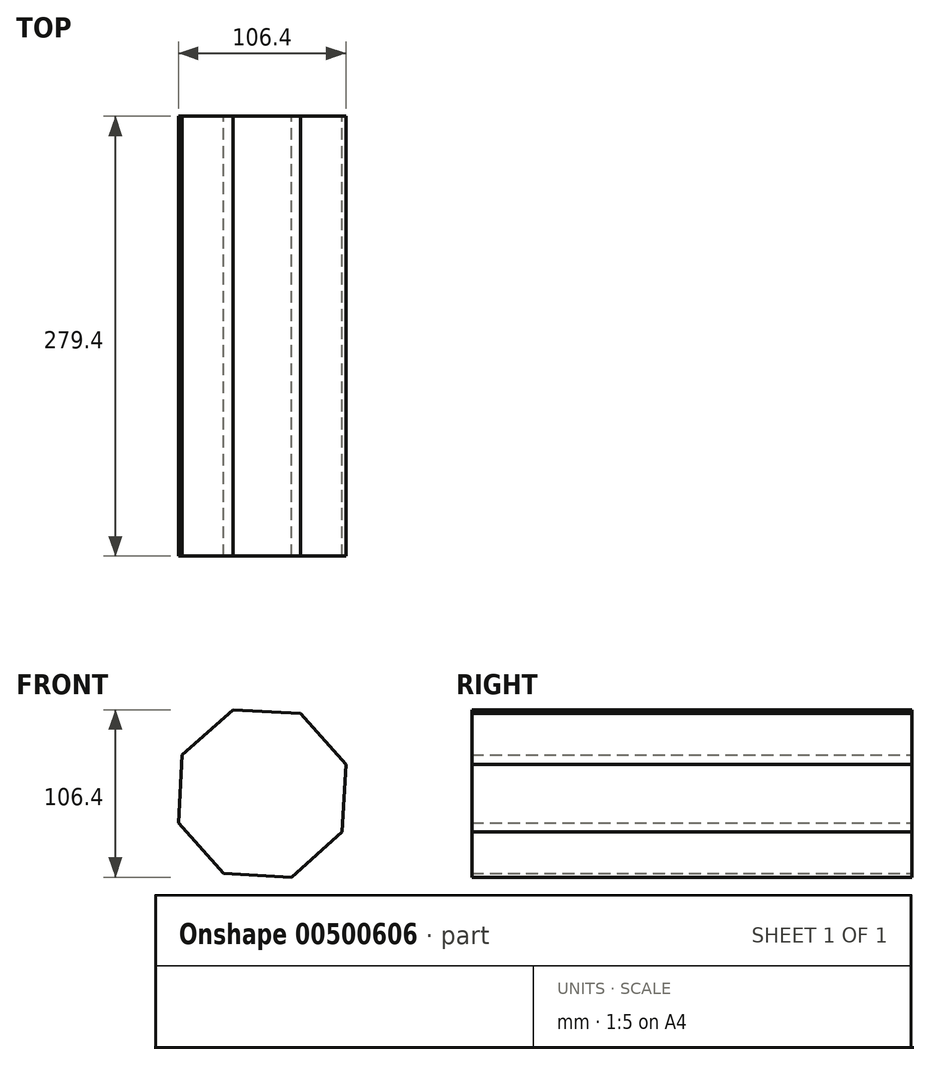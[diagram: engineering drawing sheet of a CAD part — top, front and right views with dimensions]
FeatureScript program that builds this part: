
annotation { "Feature Type Name" : "Feature", "Feature Type Description" : "" }
export const myFeature = defineFeature(function(context is Context, id is Id, definition is map)
    precondition{}
    {
        {
            var Q0;
            Q0=qCreatedBy(makeId("Front.planeOp"),FACE);
            var sketch = newSketch(context, id + "F0", { "sketchPlane" : qUnion([Q0])});
            skCircle(sketch, "E0.cCircle", {"center": v(0, 8.27) * mm, "radius": 56.35 * mm, "construction": true});
            skLineSegment(sketch, "E0.0", {"start": v(-18.58, 61.47) * mm, "end": v(24.48, 59.02) * mm});
            skLineSegment(sketch, "E0.1", {"start": v(24.48, 59.02) * mm, "end": v(53.2, 26.85) * mm});
            skLineSegment(sketch, "E0.2", {"start": v(53.2, 26.85) * mm, "end": v(50.75, -16.21) * mm});
            skLineSegment(sketch, "E0.3", {"start": v(50.75, -16.21) * mm, "end": v(18.58, -44.93) * mm});
            skLineSegment(sketch, "E0.4", {"start": v(18.58, -44.93) * mm, "end": v(-24.48, -42.48) * mm});
            skLineSegment(sketch, "E0.5", {"start": v(-24.48, -42.48) * mm, "end": v(-53.2, -10.3) * mm});
            skLineSegment(sketch, "E0.6", {"start": v(-53.2, -10.3) * mm, "end": v(-50.75, 32.75) * mm});
            skLineSegment(sketch, "E0.7", {"start": v(-50.75, 32.75) * mm, "end": v(-18.58, 61.47) * mm});
            skSolve(sketch);
        }
        {
            var Q0;
            Q0 = qSketchRegion(id + "F0", true);
            extrude(context, id + "F1", {"entities" : qUnion([Q0]), "depth" : 279.4 * mm});
        }
    });
